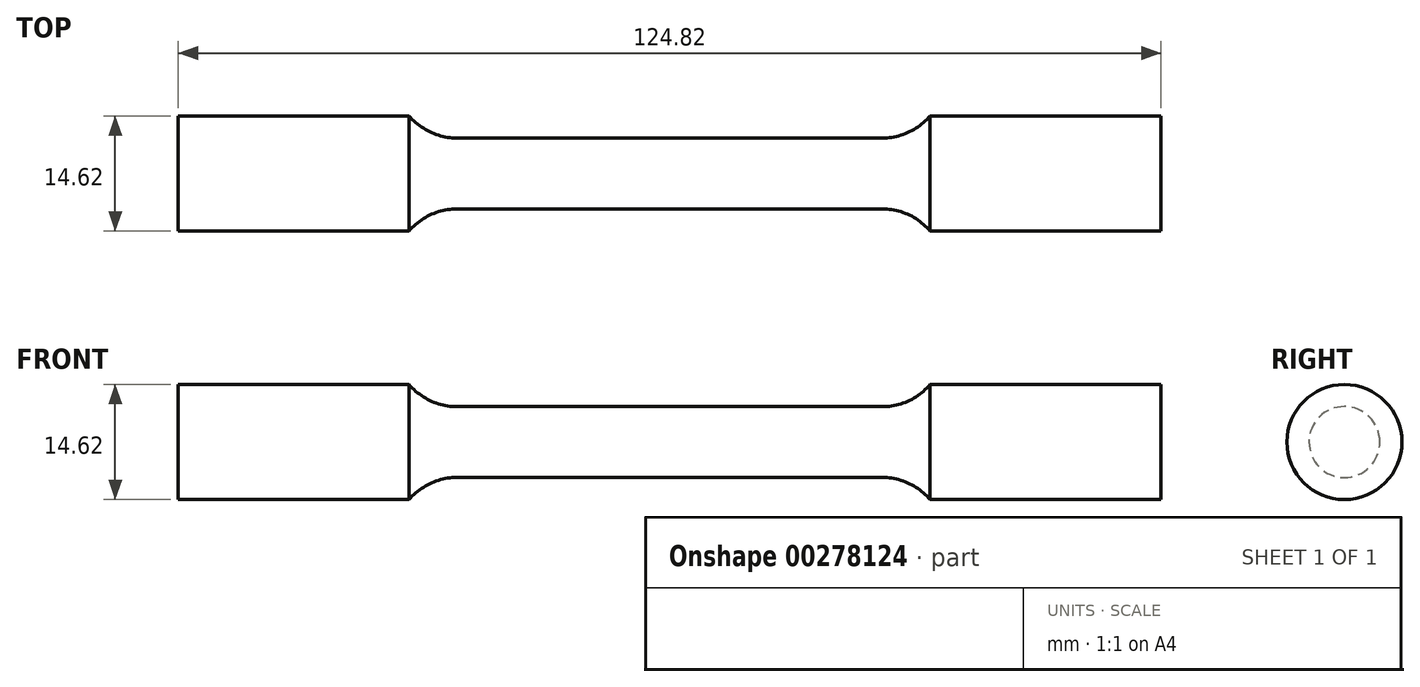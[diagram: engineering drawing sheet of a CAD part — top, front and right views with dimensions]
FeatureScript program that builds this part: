
annotation { "Feature Type Name" : "Feature", "Feature Type Description" : "" }
export const myFeature = defineFeature(function(context is Context, id is Id, definition is map)
    precondition{}
    {
        {
            var Q0;
            Q0=qCreatedBy(makeId("Front.planeOp"),FACE);
            var sketch = newSketch(context, id + "F0", { "sketchPlane" : qUnion([Q0])});
            skLineSegment(sketch, "E0", {"start": v(0, 4.5) * mm, "end": v(27, 4.5) * mm});
            skArc(sketch, "E1", {"start": v(27, 4.5) * mm, "mid": v(30.35, 5.24) * mm, "end": v(33.09, 7.3) * mm});
            skLineSegment(sketch, "E2", {"start": v(33.09, 7.3) * mm, "end": v(62.4, 7.3) * mm});
            skLineSegment(sketch, "E3", {"start": v(62.4, 7.3) * mm, "end": v(62.4, 0) * mm});
            skLineSegment(sketch, "E4.MirrorCS", {"start": v(0, 4.5) * mm, "end": v(-27, 4.5) * mm});
            skLineSegment(sketch, "E5.MirrorCS", {"start": v(-62.4, 7.3) * mm, "end": v(-62.4, 0) * mm});
            skLineSegment(sketch, "E6.MirrorCS", {"start": v(-33.09, 7.3) * mm, "end": v(-62.4, 7.3) * mm});
            skArc(sketch, "E7.MirrorCS", {"start": v(-27, 4.5) * mm, "mid": v(-30.35, 5.24) * mm, "end": v(-33.09, 7.3) * mm});
            skLineSegment(sketch, "E8", {"start": v(-62.4, 0) * mm, "end": v(62.4, 0) * mm});
            skSolve(sketch);
        }
        {
            var Q0;
            Q0 = qSketchRegion(id + "F0", true);
            var Q1;
            Q1=sQuery(id+"F0.wireOp",EDGE,"E8");
            revolve(context, id + "F1", {"entities" : qUnion([Q0]), "axis" : qUnion([Q1]), "revolveType" : RevolveType.FULL});
        }
    });
